# Revit family: Access_Door_ACUDOR_Med-Security_MS-7000
name_source: partatom
category: Doors
revit_build: Autodesk Revit 2017 (Build: 20171027_0315(x64)
units: mm (PartAtom-declared; Revit-internal decimal feet)

## family parameters
Cut with Voids When Loaded = No
Host = Face
Room Calculation Point = No
Shared = No

## types (6) — shared parameters
Analytic Construction = <None>
Default Elevation = 48 "
Description = MEDIUM SECURITY
Manufacturer = ACUDOR
Material Finish = Metal - Acudor - Stainless - Polished
URL = www.acudor.com
zero-valued in all types: Thickness, Wall Offset

## per-type parameters (varying)
| type | Code | Height | Width |
| MS-7000-1616 | 2 | 18.5 " | 18.5 " |
| MS-7000-1212 | 1 | 14.5 " | 14.5 " |
| MS-7000-1818 | 2 | 20.5 " | 20.5 " |
| MS-7000-2424 | 4 | 26.5 " | 26.5 " |
| MS-7000-2436 | 5 | 38.5 " | 26.5 " |
| MS-7000-3636 | 5 | 38.5 " | 38.5 " |

note: column(s) folded — value = type name in every type: Model

## geometry (parser evidence)
native form markers: Blend x4, Sweep x7
no freeform markers — native parametric forms only
